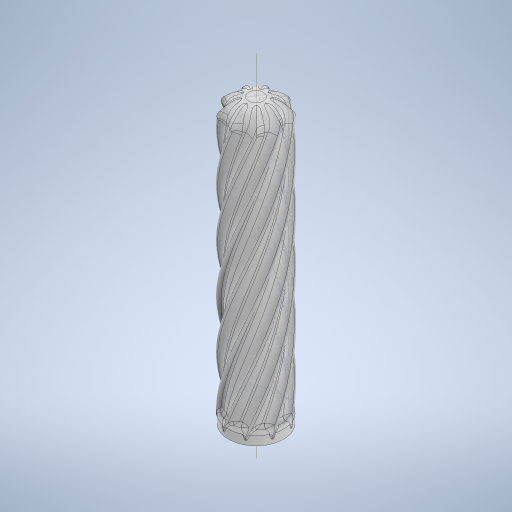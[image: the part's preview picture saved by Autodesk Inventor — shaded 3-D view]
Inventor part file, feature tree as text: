
AUTODESK INVENTOR PART (.ipt)
format: ipt  version: 2023 (Build 270158030, 158C)  size: 1,926,656 bytes
history: native  units: mm
features: fillet x7, sketch x4, projected_geometry x4, extrude x3, helix x1, pattern_circular x1
ambient origin geometry x8: Origin, YZ Plane, XZ Plane, XY Plane, X Axis, Y Axis, Z Axis, Center Point
bodies: Solid1 (feature_tree)
feature tree (20):
  extrude  "Extrusion1"  Depth=71.0mm TaperAngle=0.0deg
  extrude  "Extrusion2"  Depth=7.1mm
  extrude  "Extrusion3"  Depth=3.55mm
  fillet  "Fillet1"  Radius=13.2mm
  helix  "Coil1"  [1 undecoded]
  fillet  "Fillet3"  Radius=68.0mm
  fillet  "Fillet2"  Radius=2.6mm
  fillet  "Fillet11"  Radius=1.3mm
  pattern_circular  "Circular Pattern1"  [2 undecoded]
  fillet  "Fillet12"  Radius=1.0mm
  fillet  "Fillet8"  Radius=90.0mm
  fillet  "Fillet9"  Radius=1.0mm
  sketch  "Sketch1"  dims[d0=13.85mm d1=71.0mm d2=0.0mm]
  sketch  "Sketch2"  dims[d3=7.1mm d4=7.1mm]
  sketch  "Sketch3"  dims[d5=3.55mm d6=3.55mm d7=13.2mm d8=0.0mm d9=11.6mm d10=68.0mm d11=0.0mm d12=2.6mm d13=1.3mm]
  projected_geometry  "Projected Loop1"
  sketch  "Sketch4"  dims[d14=70.0mm d15=66.0mm d16=6.0mm d17=0.0mm d18=90.0deg d19=90.0deg d20=0.0mm d21=0.174533mm d22=3.9mm d23=2.0mm d24=1.0mm d26=90.0mm d27=360.0deg d32=1.0mm d33=0.16mm d35=2.0mm d36=0.5mm]
  projected_geometry  "Projected Loop2"
  projected_geometry  "Projected Loop3"
  projected_geometry  "Projected Loop4"
note: 3 required parameter values undecoded (feature->parameter linkage not recoverable at this tier; creation-order binding heuristic only, values carry confidence <= 0.55)
